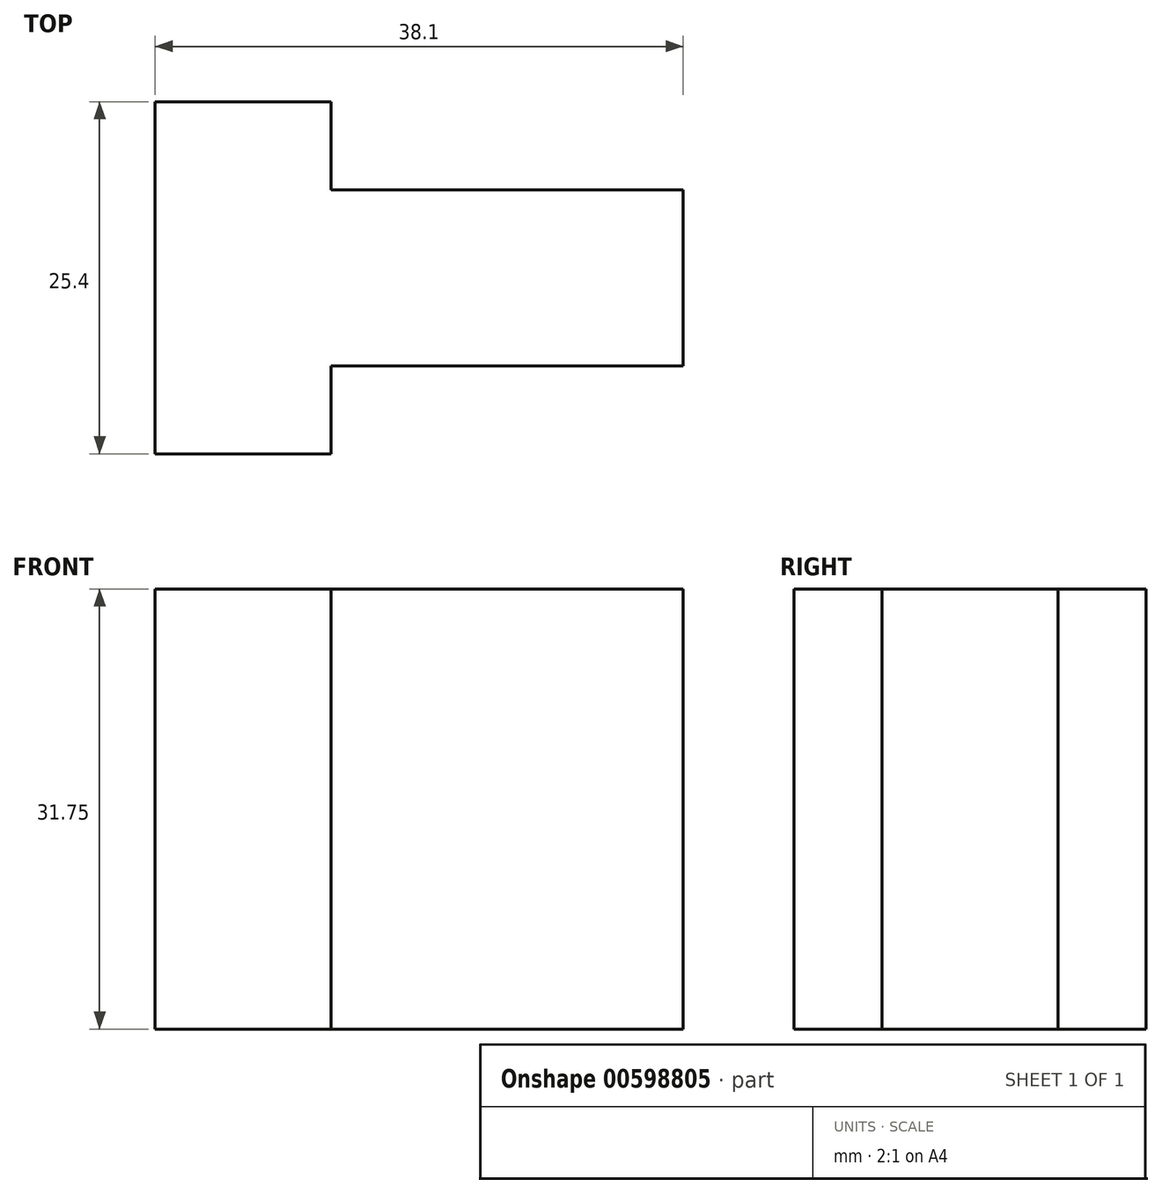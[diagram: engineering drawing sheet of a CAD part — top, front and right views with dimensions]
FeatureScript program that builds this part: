
annotation { "Feature Type Name" : "Feature", "Feature Type Description" : "" }
export const myFeature = defineFeature(function(context is Context, id is Id, definition is map)
    precondition{}
    {
        {
            var Q0;
            Q0=qCreatedBy(makeId("Top.planeOp"),FACE);
            var sketch = newSketch(context, id + "F0", { "sketchPlane" : qUnion([Q0])});
            skLineSegment(sketch, "E0", {"start": v(0, 0) * mm, "end": v(0, 25.4) * mm});
            skLineSegment(sketch, "E1", {"start": v(0, 25.4) * mm, "end": v(12.7, 25.4) * mm});
            skLineSegment(sketch, "E2", {"start": v(12.7, 25.4) * mm, "end": v(12.7, 19.05) * mm});
            skLineSegment(sketch, "E3", {"start": v(12.7, 19.05) * mm, "end": v(38.1, 19.05) * mm});
            skLineSegment(sketch, "E4", {"start": v(38.1, 19.05) * mm, "end": v(38.1, 6.35) * mm});
            skLineSegment(sketch, "E5", {"start": v(38.1, 6.35) * mm, "end": v(12.7, 6.35) * mm});
            skLineSegment(sketch, "E6", {"start": v(12.7, 6.35) * mm, "end": v(12.7, 0) * mm});
            skLineSegment(sketch, "E7", {"start": v(12.7, 0) * mm, "end": v(0, 0) * mm});
            skSolve(sketch);
        }
        {
            var Q0;
            Q0 = qSketchRegion(id + "F0", true);
            extrude(context, id + "F1", {"entities" : qUnion([Q0]), "depth" : 31.75 * mm, "offsetDistance" : 25.4 * mm});
        }
    });
